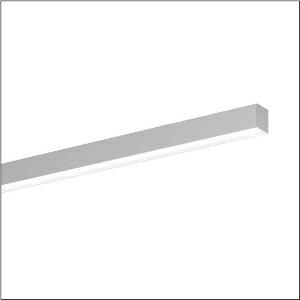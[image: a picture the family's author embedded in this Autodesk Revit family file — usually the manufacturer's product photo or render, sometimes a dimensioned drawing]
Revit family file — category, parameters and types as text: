
# Revit family: silica_r__21_51mx20db42sb_cda5
name_source: partatom
category: Lighting Fixtures
units: mm (PartAtom-declared; Revit-internal decimal feet)

## family parameters
Cut with Voids When Loaded = No
Host = Face
Light Source = No
Part Type = Normal
Room Calculation Point = No
Round Connector Dimension = Use Diameter
Shared = No

## types (1)
- --- (1 x LED, 3000 lm, 19 W, 4000K)
    Apparent Load = 19 VA
    CIE Flux Codes = 48 79 96 100 100
    Color Rendering = 80
    Color Temperature = 4000K
    Default Elevation = 1800 mm
    Description = Silica® 21, office luminaire, primary optical cover: cover, of PMMA, opal, light emission: direct distribution, primary light characteristic: symmetric, installation type: surface-mounted, LED, rated luminous flux: 3.000lm, luminous efficacy: 158lm/W, light colour: 840, colour temperature: 4000K, with terminal, 3+2-pole, max. 2.5mm², mains connection: 220..240V, AC, 50/60Hz, rated input power: 19W, luminaire housing, of aluminium, metallic grey (RAL 9006), length: 1.504mm, width: 53mm, height: 53mm, protection rating (complete): IP20, insulation class (complete): insulation class I (protective earthing), certification: CE, permissible operating ambient temperature: 0..+35°C, standard: EN 50419, packaging unit: 1 piece
    Height = 0 mm  [stored 0 ft]
    Lamp = 1 x LED
    Lamp Light Flux = 3000 lm
    Lamp Power = 19 W
    Lamp count = 1
    Length = 1504 mm
    Luminous efficacy = 158 lm/W
    Manufacturer = Siteco
    ModVariant = No
    Model = 51MX20DB42SB
    Mounting Place = Ceiling
    Mounting Type = Recessed
    Number of Poles = 1
    OnlyDefault = Yes
    Power Factor = 1
    Product Name = Silica® 21
    Product group = office luminaire | ceiling recessed
    ProductGroupID = 401
    Protection Class = Protection class I
    Protection Degree = IP 20
    RLX_Detail_Level = 1
    RLX_Emergency_Light_Flux = 0 lm
    RLX_Emergency_Type = 0
    RLX_Emergency_Type_DB = No
    RlxData = <blob elided: 26277 chars, md5=44102e6b>
    Socket = socket
    Standby Power = 0 W
    System Light Flux = 3000 lm
    System Power = 19 W
    Type Comments = factory setting: luminous flux: 100 % | dim-lin: 254 | 218 mA
    Type Image = l_1297768.jpg
    URL = http://relux.com
    VarID = @adj_048129
    Voltage = 0 V
    Weight = 0.00 kg
    Width = 53 mm

note: [stored X ft] marks values corroborated as IEEE doubles in the binary element streams (Revit-internal decimal feet)

## geometry (parser evidence)
native form markers: Blend x4, Sweep x11
no freeform markers — native parametric forms only
